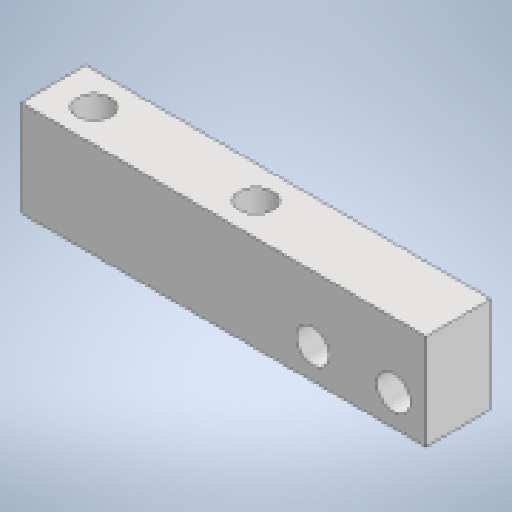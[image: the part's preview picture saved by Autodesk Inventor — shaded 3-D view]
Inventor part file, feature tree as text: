
AUTODESK INVENTOR PART (.ipt)
format: ipt  version: 2023 (Build 270158000, 158)  size: 160,768 bytes
history: native  units: mm
features: extrude x4, sketch x4
ambient origin geometry x8: Origin, YZ Plane, XZ Plane, XY Plane, X Axis, Y Axis, Z Axis, Center Point
bodies: Solid1 (feature_tree)
feature tree (8):
  extrude  "Extrusion1"  Depth=15.0mm
  extrude  "Extrusion2"  Depth=10.0mm
  extrude  "Extrusion3"  Depth=2.0mm
  extrude  "Extrusion4"  Depth=4.0mm
  sketch  "Sketch1"  dims[d0=5.9mm d1=15.0mm]
  sketch  "Sketch2"  dims[d2=4.0mm d3=0.0mm d4=10.0mm]
  sketch  "Sketch3"  dims[d5=2.5mm d6=2.0mm]
  sketch  "Sketch4"  dims[d7=2.0mm d8=2.05mm d9=2.05mm d10=8.0mm d11=0.0mm d12=10.0mm d13=4.0mm d14=0.0mm d15=2.05mm d16=5.9mm d17=4.0mm d18=4.0mm d19=5.0mm d20=2.0mm d21=2.05mm d22=2.05mm d23=4.0mm d24=0.0mm]
